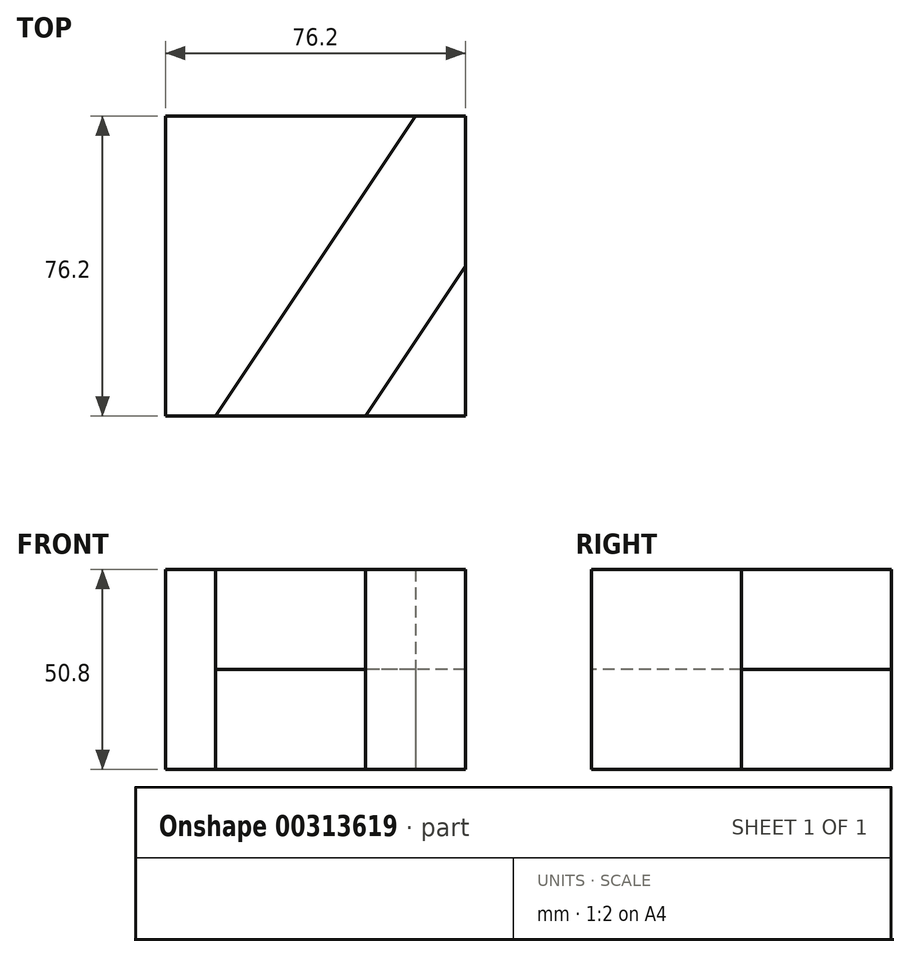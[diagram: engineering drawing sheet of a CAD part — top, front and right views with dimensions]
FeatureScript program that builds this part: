
annotation { "Feature Type Name" : "Feature", "Feature Type Description" : "" }
export const myFeature = defineFeature(function(context is Context, id is Id, definition is map)
    precondition{}
    {
        {
            var Q0;
            Q0=qCreatedBy(makeId("Top.planeOp"),FACE);
            var sketch = newSketch(context, id + "F0", { "sketchPlane" : qUnion([Q0])});
            skLineSegment(sketch, "E0", {"start": v(-42.72, -15.2) * mm, "end": v(-30.02, -15.2) * mm});
            skLineSegment(sketch, "E1", {"start": v(-42.72, -15.2) * mm, "end": v(-42.72, 61) * mm});
            skLineSegment(sketch, "E2", {"start": v(-42.72, 61) * mm, "end": v(20.78, 61) * mm});
            skLineSegment(sketch, "E3", {"start": v(20.78, 61) * mm, "end": v(-30.02, -15.2) * mm});
            skLineSegment(sketch, "E4", {"start": v(-30.02, -15.2) * mm, "end": v(8.08, -15.2) * mm});
            skLineSegment(sketch, "E5", {"start": v(8.08, -15.2) * mm, "end": v(33.48, -15.2) * mm});
            skLineSegment(sketch, "E6", {"start": v(33.48, -15.2) * mm, "end": v(33.48, 22.9) * mm});
            skLineSegment(sketch, "E7", {"start": v(33.48, 22.9) * mm, "end": v(8.08, -15.2) * mm});
            skLineSegment(sketch, "E8", {"start": v(33.48, 22.9) * mm, "end": v(33.48, 61) * mm});
            skLineSegment(sketch, "E9", {"start": v(33.48, 61) * mm, "end": v(20.78, 61) * mm});
            skSolve(sketch);
        }
        {
            var Q0;
            Q0=makeQuery(id+"F0.imprint","IMPRINT",FACE,{"disambiguationData":[TD([[makeQuery(id+"F0.imprint","IMPRINT",EDGE,{"derivedFrom":sQuery(id+"F0.wireOp",EDGE,"E5")}),1.0]])]});
            var Q1;
            Q1=makeQuery(id+"F0.imprint","IMPRINT",FACE,{"disambiguationData":[TD([[makeQuery(id+"F0.imprint","IMPRINT",EDGE,{"derivedFrom":sQuery(id+"F0.wireOp",EDGE,"E0")}),1.0]])]});
            extrude(context, id + "F1", {"entities" : qUnion([Q0, Q1]), "depth" : 50.8 * mm});
        }
        {
            var Q0;
            Q0=makeQuery(id+"F0.imprint","IMPRINT",FACE,{"disambiguationData":[TD([[makeQuery(id+"F0.imprint","IMPRINT",EDGE,{"derivedFrom":sQuery(id+"F0.wireOp",EDGE,"E3")}),1.0]])]});
            extrude(context, id + "F2", {"entities" : qUnion([Q0]), "depth" : 25.4 * mm});
        }
    });
